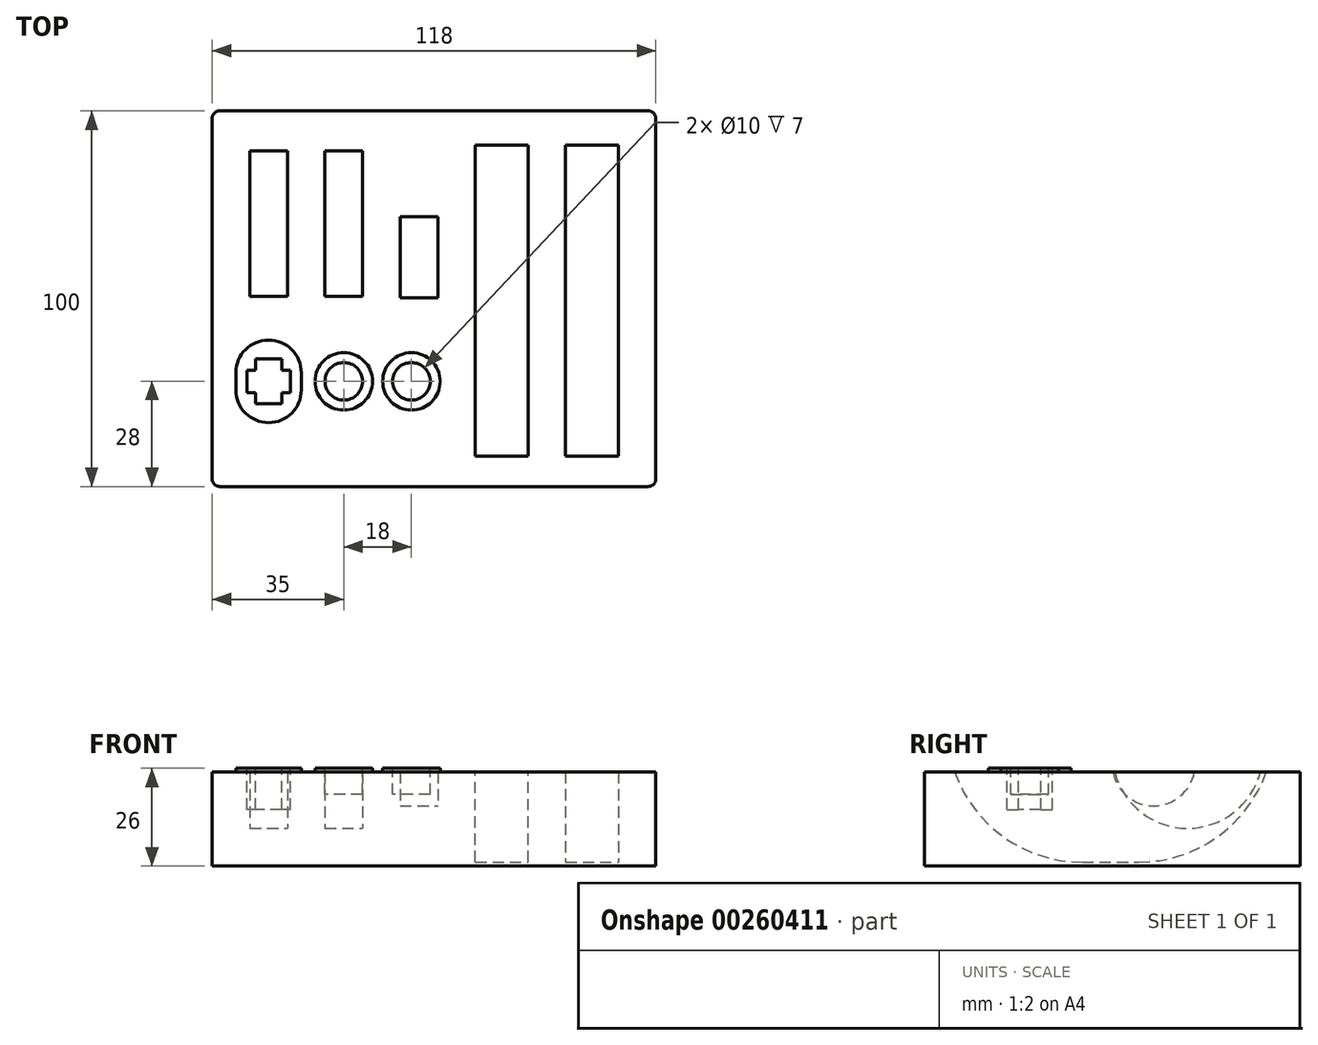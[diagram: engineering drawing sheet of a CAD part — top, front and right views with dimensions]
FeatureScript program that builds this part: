
annotation { "Feature Type Name" : "Feature", "Feature Type Description" : "" }
export const myFeature = defineFeature(function(context is Context, id is Id, definition is map)
    precondition{}
    {
        {
            var Q0;
            Q0=qCreatedBy(makeId("Top.planeOp"),FACE);
            var sketch = newSketch(context, id + "F0", { "sketchPlane" : qUnion([Q0])});
            skLineSegment(sketch, "E0.bottom", {"start": v(2, 0) * mm, "end": v(116, 0) * mm});
            skLineSegment(sketch, "E0.top", {"start": v(2, 100) * mm, "end": v(116, 100) * mm});
            skLineSegment(sketch, "E0.left", {"start": v(0, 2) * mm, "end": v(0, 98) * mm});
            skLineSegment(sketch, "E0.right", {"start": v(118, 2) * mm, "end": v(118, 98) * mm});
            skPoint(sketch, "E1.visualSharp", {"position": v(0, 100) * mm});
            skArc(sketch, "E1.filletArc", {"start": v(2, 100) * mm, "mid": v(0.59, 99.41) * mm, "end": v(0, 98) * mm});
            skPoint(sketch, "E2.visualSharp", {"position": v(0, 0) * mm});
            skArc(sketch, "E2.filletArc", {"start": v(0, 2) * mm, "mid": v(0.59, 0.59) * mm, "end": v(2, 0) * mm});
            skPoint(sketch, "E3.visualSharp", {"position": v(118, 0) * mm});
            skArc(sketch, "E3.filletArc", {"start": v(116, 0) * mm, "mid": v(117.41, 0.59) * mm, "end": v(118, 2) * mm});
            skPoint(sketch, "E4.visualSharp", {"position": v(118, 100) * mm});
            skArc(sketch, "E4.filletArc", {"start": v(118, 98) * mm, "mid": v(117.41, 99.41) * mm, "end": v(116, 100) * mm});
            skSolve(sketch);
        }
        {
            var Q0;
            Q0=makeQuery(id+"F0.imprint","IMPRINT",FACE,{"disambiguationData":[TD([[makeQuery(id+"F0.imprint","IMPRINT",EDGE,{"derivedFrom":sQuery(id+"F0.wireOp",EDGE,"E0.bottom")}),1.0]])]});
            extrude(context, id + "F1", {"entities" : qUnion([Q0]), "depth" : 25 * mm});
        }
        {
            var Q0;
            Q0=makeQuery(id+"F1.opExtrude","CAP_FACE",FACE,{"disambiguationData":[OSD([sQuery(id+"F0.wireOp",EDGE,"E0.bottom"),sQuery(id+"F0.wireOp",EDGE,"E0.top"),sQuery(id+"F0.wireOp",EDGE,"E0.left"),sQuery(id+"F0.wireOp",EDGE,"E0.right"),sQuery(id+"F0.wireOp",EDGE,"E1.filletArc"),sQuery(id+"F0.wireOp",EDGE,"E2.filletArc"),sQuery(id+"F0.wireOp",EDGE,"E3.filletArc"),sQuery(id+"F0.wireOp",EDGE,"E4.filletArc")])],"isStart":false});
            var sketch = newSketch(context, id + "F2", { "sketchPlane" : qUnion([Q0])});
            skLineSegment(sketch, "E5.bottom", {"start": v(0, 0) * mm, "end": v(15, 0) * mm, "construction": true});
            skLineSegment(sketch, "E5.top", {"start": v(0, 28) * mm, "end": v(15, 28) * mm, "construction": true});
            skLineSegment(sketch, "E5.left", {"start": v(0, 0) * mm, "end": v(0, 28) * mm, "construction": true});
            skLineSegment(sketch, "E5.right", {"start": v(15, 0) * mm, "end": v(15, 28) * mm, "construction": true});
            skLineSegment(sketch, "E6", {"start": v(15, 28) * mm, "end": v(35, 28) * mm, "construction": true});
            skCircle(sketch, "E7", {"center": v(35, 28) * mm, "radius": 7.65 * mm});
            skLineSegment(sketch, "E8", {"start": v(15, 25.7) * mm, "end": v(15, 28) * mm, "construction": true});
            skLineSegment(sketch, "E9", {"start": v(15, 25.7) * mm, "end": v(15, 30.3) * mm, "construction": true});
            skArc(sketch, "E10", {"start": v(23.7, 30.3) * mm, "mid": v(15, 39) * mm, "end": v(6.3, 30.3) * mm});
            skArc(sketch, "E11", {"start": v(6.3, 25.7) * mm, "mid": v(15, 17) * mm, "end": v(23.7, 25.7) * mm});
            skLineSegment(sketch, "E12", {"start": v(23.7, 30.3) * mm, "end": v(23.7, 25.7) * mm});
            skLineSegment(sketch, "E13", {"start": v(23.7, 25.7) * mm, "end": v(6.3, 25.7) * mm, "construction": true});
            skLineSegment(sketch, "E14", {"start": v(6.3, 25.7) * mm, "end": v(6.3, 30.3) * mm});
            skLineSegment(sketch, "E15", {"start": v(35, 28) * mm, "end": v(53, 28) * mm, "construction": true});
            skCircle(sketch, "E16", {"center": v(53, 28) * mm, "radius": 7.65 * mm});
            skSolve(sketch);
        }
        {
            var Q0;
            Q0 = qSketchRegion(id + "F2", true);
            extrude(context, id + "F3", {"entities" : qUnion([Q0]), "operationType" : NewBodyOperationType.ADD, "depth" : 1 * mm});
        }
        {
            var Q0;
            Q0=makeQuery(id+"F3.opExtrude","CAP_FACE",FACE,{"disambiguationData":[OSD([sQuery(id+"F2.wireOp",EDGE,"E10"),sQuery(id+"F2.wireOp",EDGE,"E11"),sQuery(id+"F2.wireOp",EDGE,"E12"),sQuery(id+"F2.wireOp",EDGE,"E14")])],"isStart":false});
            var sketch = newSketch(context, id + "F4", { "sketchPlane" : qUnion([Q0])});
            skLineSegment(sketch, "E17.0.0", {"start": v(6.3, 30.3) * mm, "end": v(6.3, 25.7) * mm});
            skArc(sketch, "E17.0.1", {"start": v(6.3, 25.7) * mm, "mid": v(15, 17) * mm, "end": v(23.7, 25.7) * mm});
            skLineSegment(sketch, "E17.0.2", {"start": v(23.7, 25.7) * mm, "end": v(23.7, 30.3) * mm});
            skArc(sketch, "E17.0.3", {"start": v(23.7, 30.3) * mm, "mid": v(15, 39) * mm, "end": v(6.3, 30.3) * mm});
            skLineSegment(sketch, "E18", {"start": v(6.3, 30.3) * mm, "end": v(23.7, 25.7) * mm, "construction": true});
            skLineSegment(sketch, "E19.bottom", {"start": v(20.75, 31) * mm, "end": v(18.5, 31) * mm});
            skLineSegment(sketch, "E19.top", {"start": v(20.75, 25) * mm, "end": v(18.5, 25) * mm});
            skLineSegment(sketch, "E19.left", {"start": v(20.75, 31) * mm, "end": v(20.75, 25) * mm});
            skLineSegment(sketch, "E19.right", {"start": v(9.25, 31) * mm, "end": v(9.25, 25) * mm});
            skPoint(sketch, "E19.middle", {"position": v(15, 28) * mm});
            skLineSegment(sketch, "E20.bottom", {"start": v(18.5, 22) * mm, "end": v(11.5, 22) * mm});
            skLineSegment(sketch, "E20.top", {"start": v(18.5, 34) * mm, "end": v(11.5, 34) * mm});
            skLineSegment(sketch, "E20.left", {"start": v(18.5, 22) * mm, "end": v(18.5, 25) * mm});
            skLineSegment(sketch, "E20.right", {"start": v(11.5, 22) * mm, "end": v(11.5, 25) * mm});
            skLineSegment(sketch, "E21.trimOffspring", {"start": v(11.5, 31) * mm, "end": v(9.25, 31) * mm});
            skLineSegment(sketch, "E22.trimOffspring", {"start": v(11.5, 25) * mm, "end": v(9.25, 25) * mm});
            skLineSegment(sketch, "E23.trimOffspring", {"start": v(11.5, 31) * mm, "end": v(11.5, 34) * mm});
            skLineSegment(sketch, "E24.trimOffspring", {"start": v(18.5, 31) * mm, "end": v(18.5, 34) * mm});
            skSolve(sketch);
        }
        {
            var Q0;
            Q0=makeQuery(id+"F4.imprint","IMPRINT",FACE,{"disambiguationData":[TD([[makeQuery(id+"F4.imprint","IMPRINT",EDGE,{"derivedFrom":sQuery(id+"F4.wireOp",EDGE,"E19.bottom")}),1.0]])]});
            extrude(context, id + "F5", {"entities" : qUnion([Q0]), "operationType" : NewBodyOperationType.REMOVE, "oppositeDirection" : true, "depth" : 11 * mm});
        }
        {
            var Q0;
            Q0=makeQuery(id+"F1.opExtrude","CAP_FACE",FACE,{"disambiguationData":[OSD([sQuery(id+"F0.wireOp",EDGE,"E0.bottom"),sQuery(id+"F0.wireOp",EDGE,"E0.top"),sQuery(id+"F0.wireOp",EDGE,"E0.left"),sQuery(id+"F0.wireOp",EDGE,"E0.right"),sQuery(id+"F0.wireOp",EDGE,"E1.filletArc"),sQuery(id+"F0.wireOp",EDGE,"E2.filletArc"),sQuery(id+"F0.wireOp",EDGE,"E3.filletArc"),sQuery(id+"F0.wireOp",EDGE,"E4.filletArc")])],"isStart":false});
            cPlane(context, id + "F6", {"entities" : qUnion([Q0]), "cplaneType" : CPlaneType.OFFSET, "offset" : 5 * mm, "width" : 150 * mm, "height" : 150 * mm});
        }
        {
            var Q0;
            Q0=qCreatedBy(id+"F6.planeOp",FACE);
            var sketch = newSketch(context, id + "F7", { "sketchPlane" : qUnion([Q0])});
            skLineSegment(sketch, "E25.bottom", {"start": v(0, 0) * mm, "end": v(10, 0) * mm, "construction": true});
            skLineSegment(sketch, "E25.top", {"start": v(0, 90) * mm, "end": v(10, 90) * mm, "construction": true});
            skLineSegment(sketch, "E25.left", {"start": v(0, 0) * mm, "end": v(0, 90) * mm, "construction": true});
            skLineSegment(sketch, "E25.right", {"start": v(10, 0) * mm, "end": v(10, 90) * mm, "construction": true});
            skLineSegment(sketch, "E26.bottom", {"start": v(10, 90) * mm, "end": v(20, 90) * mm});
            skLineSegment(sketch, "E26.top", {"start": v(10, 70) * mm, "end": v(20, 70) * mm});
            skLineSegment(sketch, "E26.left", {"start": v(10, 90) * mm, "end": v(10, 70) * mm});
            skLineSegment(sketch, "E26.right", {"start": v(20, 90) * mm, "end": v(20, 70) * mm});
            skLineSegment(sketch, "E27", {"start": v(20, 70) * mm, "end": v(30, 70) * mm, "construction": true});
            skLineSegment(sketch, "E28.bottom", {"start": v(30, 70) * mm, "end": v(40, 70) * mm});
            skLineSegment(sketch, "E28.top", {"start": v(30, 90) * mm, "end": v(40, 90) * mm});
            skLineSegment(sketch, "E28.left", {"start": v(30, 70) * mm, "end": v(30, 90) * mm});
            skLineSegment(sketch, "E28.right", {"start": v(40, 70) * mm, "end": v(40, 90) * mm});
            skSolve(sketch);
        }
        {
            var Q0;
            Q0 = qSketchRegion(id + "F7", true);
            var Q1;
            Q1=sQuery(id+"F7.wireOp",EDGE,"E27");
            revolve(context, id + "F8", {"operationType" : NewBodyOperationType.REMOVE, "entities" : qUnion([Q0]), "axis" : qUnion([Q1]), "revolveType" : RevolveType.FULL, "oppositeDirection" : true});
        }
        {
            var Q0;
            Q0=makeQuery(id+"F1.opExtrude","CAP_FACE",FACE,{"disambiguationData":[OSD([sQuery(id+"F0.wireOp",EDGE,"E0.bottom"),sQuery(id+"F0.wireOp",EDGE,"E0.top"),sQuery(id+"F0.wireOp",EDGE,"E0.left"),sQuery(id+"F0.wireOp",EDGE,"E0.right"),sQuery(id+"F0.wireOp",EDGE,"E1.filletArc"),sQuery(id+"F0.wireOp",EDGE,"E2.filletArc"),sQuery(id+"F0.wireOp",EDGE,"E3.filletArc"),sQuery(id+"F0.wireOp",EDGE,"E4.filletArc")])],"isStart":false});
            cPlane(context, id + "F9", {"entities" : qUnion([Q0]), "cplaneType" : CPlaneType.OFFSET, "offset" : 2 * mm, "width" : 150 * mm, "height" : 150 * mm});
        }
        {
            var Q0;
            Q0=qCreatedBy(id+"F9.planeOp",FACE);
            var sketch = newSketch(context, id + "F10", { "sketchPlane" : qUnion([Q0])});
            skLineSegment(sketch, "E29.bottom", {"start": v(0, 0) * mm, "end": v(50, 0) * mm, "construction": true});
            skLineSegment(sketch, "E29.top", {"start": v(0, 50) * mm, "end": v(50, 50) * mm, "construction": true});
            skLineSegment(sketch, "E29.left", {"start": v(0, 0) * mm, "end": v(0, 50) * mm, "construction": true});
            skLineSegment(sketch, "E29.right", {"start": v(50, 0) * mm, "end": v(50, 50) * mm, "construction": true});
            skLineSegment(sketch, "E30.bottom", {"start": v(50, 50) * mm, "end": v(60, 50) * mm});
            skLineSegment(sketch, "E30.top", {"start": v(50, 61) * mm, "end": v(60, 61) * mm});
            skLineSegment(sketch, "E30.left", {"start": v(50, 50) * mm, "end": v(50, 61) * mm});
            skLineSegment(sketch, "E30.right", {"start": v(60, 50) * mm, "end": v(60, 61) * mm});
            skSolve(sketch);
        }
        {
            var Q0;
            Q0=makeQuery(id+"F10.imprint","IMPRINT",FACE,{"disambiguationData":[TD([[makeQuery(id+"F10.imprint","IMPRINT",EDGE,{"derivedFrom":sQuery(id+"F10.wireOp",EDGE,"E30.bottom")}),1.0]])]});
            var Q1;
            Q1=sQuery(id+"F10.wireOp",EDGE,"E30.top");
            revolve(context, id + "F11", {"operationType" : NewBodyOperationType.REMOVE, "entities" : qUnion([Q0]), "axis" : qUnion([Q1]), "revolveType" : RevolveType.FULL, "oppositeDirection" : true});
        }
        {
            var Q0;
            Q0=makeQuery(id+"F1.opExtrude","SWEPT_FACE",FACE,{"disambiguationData":[OSD([sQuery(id+"F0.wireOp",EDGE,"E0.right")])]});
            var sketch = newSketch(context, id + "F12", { "sketchPlane" : qUnion([Q0])});
            skLineSegment(sketch, "E31.0", {"start": v(100, 25) * mm, "end": v(100, 0) * mm, "construction": true});
            skLineSegment(sketch, "E32", {"start": v(100, 25) * mm, "end": v(92, 25) * mm, "construction": true});
            skLineSegment(sketch, "E33", {"start": v(92, 25) * mm, "end": v(57, 25) * mm, "construction": true});
            skLineSegment(sketch, "E34", {"start": v(57, 25) * mm, "end": v(57, 37) * mm, "construction": true});
            skLineSegment(sketch, "E35", {"start": v(57, 37) * mm, "end": v(42, 37) * mm, "construction": true});
            skArc(sketch, "E36", {"start": v(57, 1) * mm, "mid": v(92.8, 40.77) * mm, "end": v(49.5, 72.21) * mm});
            skArc(sketch, "E37", {"start": v(49.5, 72.21) * mm, "mid": v(6.2, 40.77) * mm, "end": v(42, 1) * mm});
            skLineSegment(sketch, "E38", {"start": v(42, 37) * mm, "end": v(42, 1) * mm, "construction": true});
            skLineSegment(sketch, "E39", {"start": v(42, 1) * mm, "end": v(57, 1) * mm});
            skSolve(sketch);
        }
        {
            var Q0;
            Q0 = qSketchRegion(id + "F12", true);
            extrude(context, id + "F13", {"entities" : qUnion([Q0]), "operationType" : NewBodyOperationType.REMOVE, "oppositeDirection" : true, "depth" : 24 * mm, "hasSecondDirection" : true, "secondDirectionOppositeDirection" : true, "secondDirectionDepth" : 10 * mm});
        }
        {
            var Q0;
            {var subQ0=sQuery(id+"F12.wireOp",EDGE,"E39");Q0=makeQuery(id+"F12.imprint","IMPRINT",FACE,{"disambiguationData":[TD([[makeQuery(id+"F12.imprint","IMPRINT",EDGE,{"derivedFrom":subQ0}),1.0]])]});}
            extrude(context, id + "F14", {"entities" : qUnion([Q0]), "operationType" : NewBodyOperationType.REMOVE, "oppositeDirection" : true, "depth" : 48 * mm, "hasSecondDirection" : true, "secondDirectionOppositeDirection" : true, "secondDirectionDepth" : 34 * mm});
        }
        {
            var Q0;
            Q0=makeQuery(id+"F3.opExtrude","CAP_FACE",FACE,{"disambiguationData":[OSD([sQuery(id+"F2.wireOp",EDGE,"E7")])],"isStart":false});
            var sketch = newSketch(context, id + "F15", { "sketchPlane" : qUnion([Q0])});
            skCircle(sketch, "E40.0.0", {"center": v(53, 28) * mm, "radius": 7.65 * mm});
            skCircle(sketch, "E41.0.0", {"center": v(35, 28) * mm, "radius": 7.65 * mm});
            skCircle(sketch, "E42", {"center": v(35, 28) * mm, "radius": 5 * mm});
            skCircle(sketch, "E43", {"center": v(53, 28) * mm, "radius": 5 * mm});
            skSolve(sketch);
        }
        {
            var Q0;
            Q0=makeQuery(id+"F15.imprint","IMPRINT",FACE,{"disambiguationData":[TD([[makeQuery(id+"F15.imprint","IMPRINT",EDGE,{"derivedFrom":sQuery(id+"F15.wireOp",EDGE,"E42")}),1.0]])]});
            var Q1;
            Q1=makeQuery(id+"F15.imprint","IMPRINT",FACE,{"disambiguationData":[TD([[makeQuery(id+"F15.imprint","IMPRINT",EDGE,{"derivedFrom":sQuery(id+"F15.wireOp",EDGE,"E43")}),1.0]])]});
            extrude(context, id + "F16", {"entities" : qUnion([Q0, Q1]), "operationType" : NewBodyOperationType.REMOVE, "oppositeDirection" : true, "depth" : 7 * mm});
        }
    });
